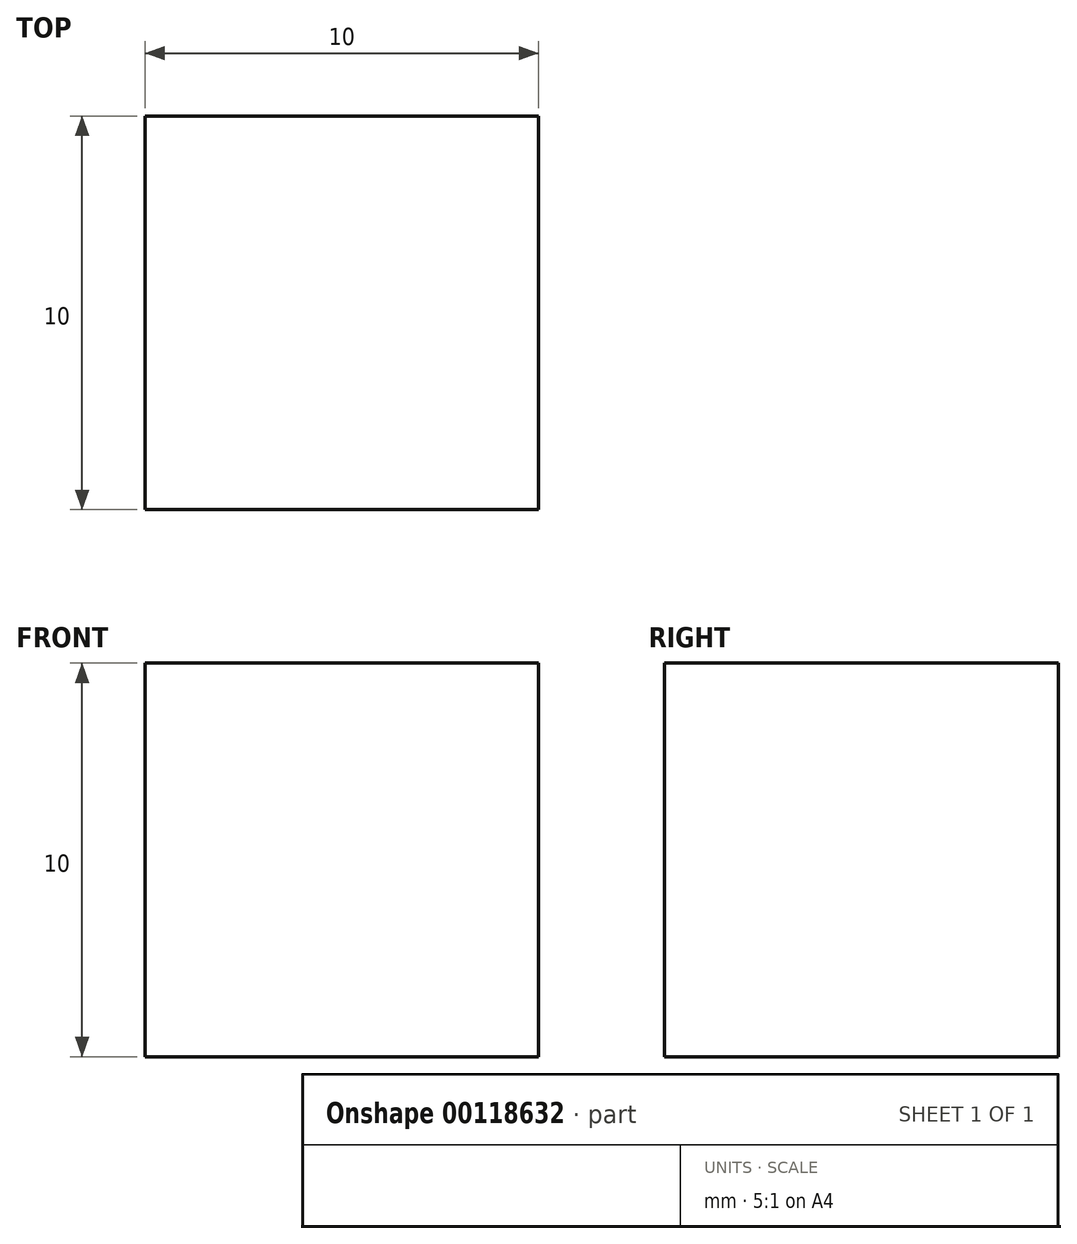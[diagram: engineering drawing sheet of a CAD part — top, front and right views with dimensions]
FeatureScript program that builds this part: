
annotation { "Feature Type Name" : "Feature", "Feature Type Description" : "" }
export const myFeature = defineFeature(function(context is Context, id is Id, definition is map)
    precondition{}
    {
        {
            var Q0;
            Q0=qCreatedBy(makeId("Top.planeOp"),FACE);
            var sketch = newSketch(context, id + "F0", { "sketchPlane" : qUnion([Q0])});
            skLineSegment(sketch, "E0.bottom", {"start": v(5, -5) * mm, "end": v(-5, -5) * mm});
            skLineSegment(sketch, "E0.top", {"start": v(5, 5) * mm, "end": v(-5, 5) * mm});
            skLineSegment(sketch, "E0.left", {"start": v(5, -5) * mm, "end": v(5, 5) * mm});
            skLineSegment(sketch, "E0.right", {"start": v(-5, -5) * mm, "end": v(-5, 5) * mm});
            skPoint(sketch, "E0.middle", {"position": v(0, 0) * mm});
            skSolve(sketch);
        }
        {
            var Q0;
            Q0=qSketchRegion(id+"F0",true);
            extrude(context, id + "F1", {"entities" : qUnion([Q0]), "depth" : 10 * mm});
        }
    });
